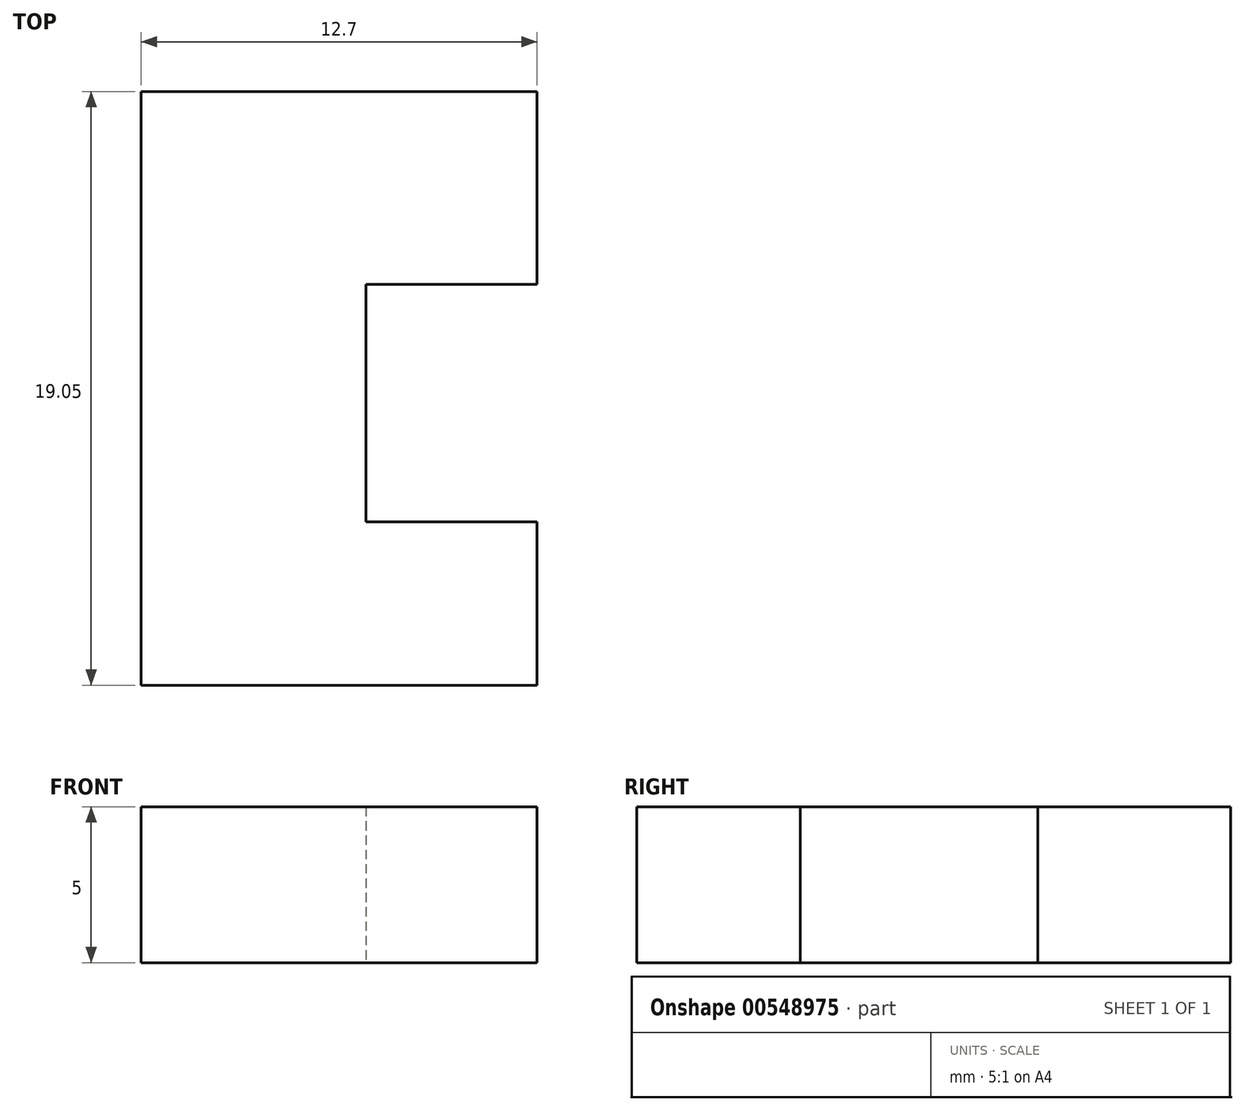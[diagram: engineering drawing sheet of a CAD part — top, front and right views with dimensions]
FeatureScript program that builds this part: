
annotation { "Feature Type Name" : "Feature", "Feature Type Description" : "" }
export const myFeature = defineFeature(function(context is Context, id is Id, definition is map)
    precondition{}
    {
        {
            var Q0;
            Q0=qCreatedBy(makeId("Top.planeOp"),FACE);
            var sketch = newSketch(context, id + "F0", { "sketchPlane" : qUnion([Q0])});
            skLineSegment(sketch, "E0.bottom", {"start": v(-1.44, -9.44) * mm, "end": v(11.26, -9.44) * mm});
            skLineSegment(sketch, "E0.top", {"start": v(-1.44, 9.6) * mm, "end": v(11.26, 9.6) * mm});
            skLineSegment(sketch, "E0.left", {"start": v(-1.44, -9.44) * mm, "end": v(-1.44, 9.6) * mm});
            skLineSegment(sketch, "E0.right", {"start": v(11.26, -9.44) * mm, "end": v(11.26, 9.6) * mm});
            skLineSegment(sketch, "E1", {"start": v(11.26, -4.2) * mm, "end": v(5.77, -4.2) * mm});
            skLineSegment(sketch, "E2", {"start": v(5.77, -4.2) * mm, "end": v(5.77, 3.43) * mm});
            skLineSegment(sketch, "E3", {"start": v(5.77, 3.43) * mm, "end": v(11.26, 3.43) * mm});
            skSolve(sketch);
        }
        {
            var Q0;
            {var subQ1=sQuery(id+"F0.wireOp",EDGE,"E0.bottom");Q0=makeQuery(id+"F0.imprint","IMPRINT",FACE,{"disambiguationData":[TD([[makeQuery(id+"F0.imprint","IMPRINT",EDGE,{"derivedFrom":subQ1}),1.0]])]});}
            extrude(context, id + "F1", {"entities" : qUnion([Q0]), "depth" : 5 * mm, "offsetDistance" : 25.4 * mm});
        }
    });
